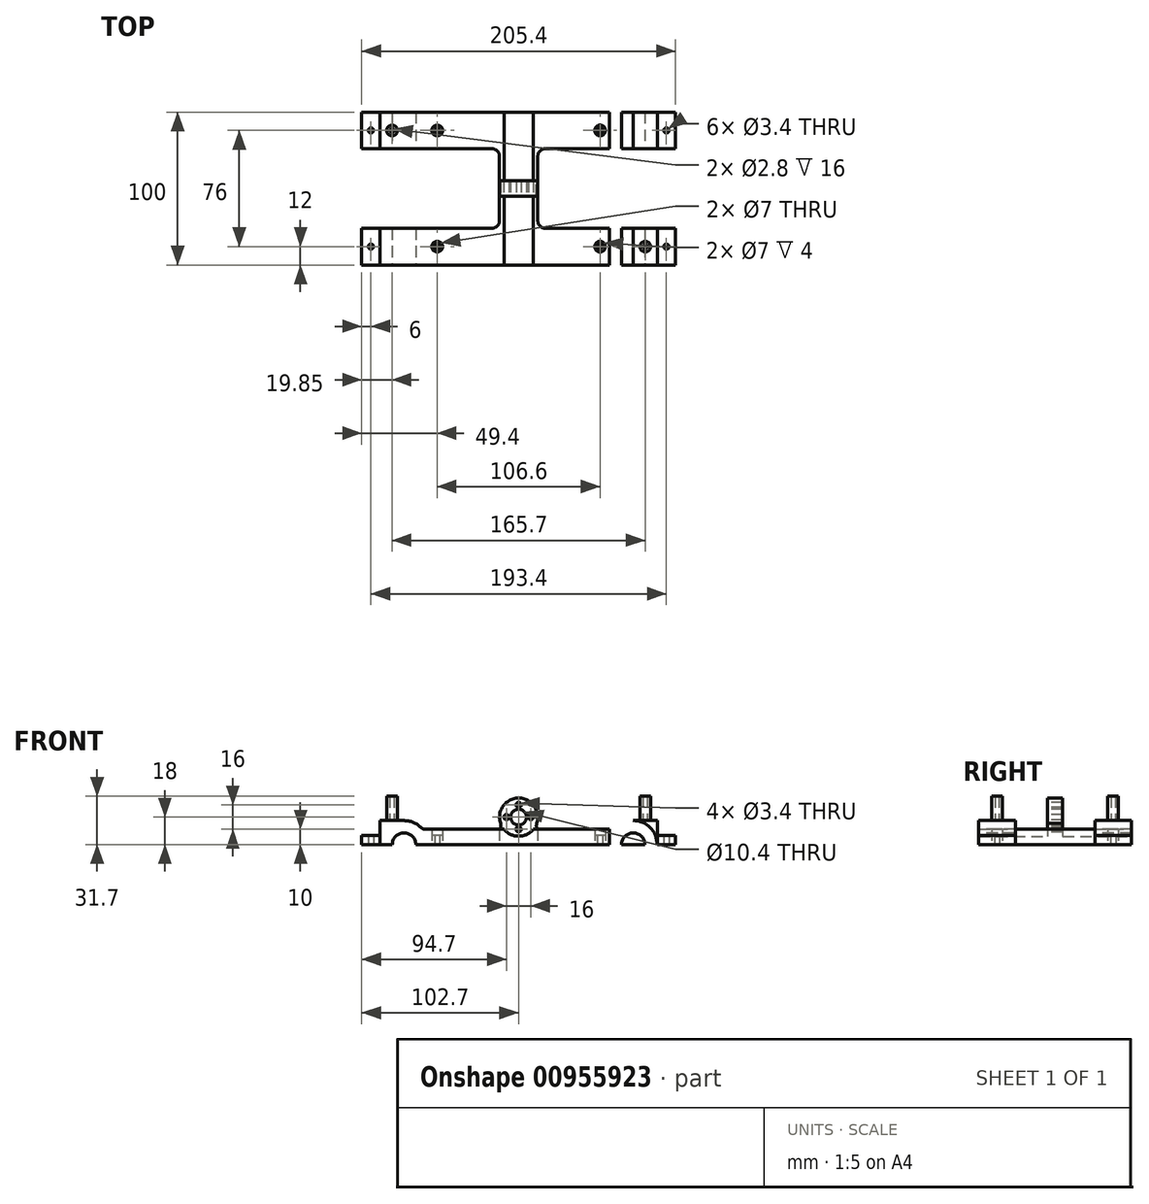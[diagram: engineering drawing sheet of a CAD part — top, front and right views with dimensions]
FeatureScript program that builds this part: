
annotation { "Feature Type Name" : "Feature", "Feature Type Description" : "" }
export const myFeature = defineFeature(function(context is Context, id is Id, definition is map)
    precondition{}
    {
        {
            var Q0;
            Q0=qCreatedBy(makeId("Top.planeOp"),FACE);
            var sketch = newSketch(context, id + "F0", { "sketchPlane" : qUnion([Q0])});
            skLineSegment(sketch, "E0", {"start": v(0, 0) * mm, "end": v(0, 50) * mm, "construction": true});
            skLineSegment(sketch, "E1", {"start": v(0, 0) * mm, "end": v(0, -50) * mm, "construction": true});
            skLineSegment(sketch, "E2", {"start": v(0, 50) * mm, "end": v(-59.3, 50) * mm});
            skLineSegment(sketch, "E3", {"start": v(-59.3, 50) * mm, "end": v(-59.3, 26) * mm});
            skLineSegment(sketch, "E4.bottom", {"start": v(-59.3, 26) * mm, "end": v(-90.7, 26) * mm});
            skLineSegment(sketch, "E4.top", {"start": v(-59.3, 50) * mm, "end": v(-90.7, 50) * mm});
            skLineSegment(sketch, "E4.left", {"start": v(-59.3, 26) * mm, "end": v(-59.3, 50) * mm});
            skLineSegment(sketch, "E4.right", {"start": v(-90.7, 26) * mm, "end": v(-90.7, 50) * mm});
            skLineSegment(sketch, "E5", {"start": v(-59.3, 26) * mm, "end": v(-12.5, 26) * mm});
            skLineSegment(sketch, "E6", {"start": v(0, 0) * mm, "end": v(-12.5, 0) * mm, "construction": true});
            skLineSegment(sketch, "E7", {"start": v(-12.5, 0) * mm, "end": v(-12.5, 26) * mm});
            skLineSegment(sketch, "E8.MirrorCS", {"start": v(59.3, 50) * mm, "end": v(90.7, 50) * mm});
            skLineSegment(sketch, "E9.MirrorCS", {"start": v(90.7, 26) * mm, "end": v(90.7, 50) * mm});
            skLineSegment(sketch, "E10.MirrorCS", {"start": v(59.3, 26) * mm, "end": v(90.7, 26) * mm});
            skLineSegment(sketch, "E11.MirrorCS", {"start": v(59.3, 26) * mm, "end": v(59.3, 50) * mm});
            skLineSegment(sketch, "E12.MirrorCS", {"start": v(59.3, 26) * mm, "end": v(12.5, 26) * mm});
            skLineSegment(sketch, "E13.MirrorCS", {"start": v(0, 50) * mm, "end": v(59.3, 50) * mm});
            skLineSegment(sketch, "E14.MirrorCS", {"start": v(12.5, 0) * mm, "end": v(12.5, 26) * mm});
            skLineSegment(sketch, "E15.MirrorCS", {"start": v(-12.5, 0) * mm, "end": v(-12.5, -26) * mm});
            skLineSegment(sketch, "E16.MirrorCS", {"start": v(-59.3, -26) * mm, "end": v(-12.5, -26) * mm});
            skLineSegment(sketch, "E17.MirrorCS", {"start": v(-59.3, -26) * mm, "end": v(-90.7, -26) * mm});
            skLineSegment(sketch, "E18.MirrorCS", {"start": v(-90.7, -26) * mm, "end": v(-90.7, -50) * mm});
            skLineSegment(sketch, "E19.MirrorCS", {"start": v(-59.3, -50) * mm, "end": v(-90.7, -50) * mm});
            skLineSegment(sketch, "E20.MirrorCS", {"start": v(-59.3, -26) * mm, "end": v(-59.3, -50) * mm});
            skLineSegment(sketch, "E21.MirrorCS", {"start": v(0, -50) * mm, "end": v(-59.3, -50) * mm});
            skLineSegment(sketch, "E22.MirrorCS", {"start": v(0, -50) * mm, "end": v(59.3, -50) * mm});
            skLineSegment(sketch, "E23.MirrorCS", {"start": v(59.3, -26) * mm, "end": v(12.5, -26) * mm});
            skLineSegment(sketch, "E24.MirrorCS", {"start": v(12.5, 0) * mm, "end": v(12.5, -26) * mm});
            skLineSegment(sketch, "E25.MirrorCS", {"start": v(59.3, -26) * mm, "end": v(90.7, -26) * mm});
            skLineSegment(sketch, "E26.MirrorCS", {"start": v(59.3, -26) * mm, "end": v(59.3, -50) * mm});
            skLineSegment(sketch, "E27.MirrorCS", {"start": v(59.3, -50) * mm, "end": v(90.7, -50) * mm});
            skLineSegment(sketch, "E28.MirrorCS", {"start": v(90.7, -26) * mm, "end": v(90.7, -50) * mm});
            skLineSegment(sketch, "E29.bottom", {"start": v(-12.5, 5) * mm, "end": v(12.5, 5) * mm});
            skLineSegment(sketch, "E29.top", {"start": v(-12.5, -5) * mm, "end": v(12.5, -5) * mm});
            skLineSegment(sketch, "E29.left", {"start": v(-12.5, 5) * mm, "end": v(-12.5, -5) * mm});
            skLineSegment(sketch, "E29.right", {"start": v(12.5, 5) * mm, "end": v(12.5, -5) * mm});
            skPoint(sketch, "E29.middle", {"position": v(0, 0) * mm});
            skLineSegment(sketch, "E30.bottom", {"start": v(-90.7, 50) * mm, "end": v(-99.7, 50) * mm});
            skLineSegment(sketch, "E30.top", {"start": v(-90.7, 26) * mm, "end": v(-99.7, 26) * mm});
            skLineSegment(sketch, "E30.left", {"start": v(-90.7, 50) * mm, "end": v(-90.7, 26) * mm});
            skCircle(sketch, "E31", {"center": v(-96.7, 38) * mm, "radius": 1.7 * mm});
            skPoint(sketch, "E31.centerSnap0", {"position": v(-90.7, 38) * mm});
            skPoint(sketch, "E31.centerSnap1", {"position": v(-96.7, 50) * mm});
            skLineSegment(sketch, "E32.MirrorCS", {"start": v(90.7, 50) * mm, "end": v(99.7, 50) * mm});
            skLineSegment(sketch, "E33.MirrorCS", {"start": v(90.7, 26) * mm, "end": v(99.7, 26) * mm});
            skLineSegment(sketch, "E34.MirrorCS", {"start": v(90.7, 50) * mm, "end": v(90.7, 26) * mm});
            skCircle(sketch, "E35.MirrorC", {"center": v(96.7, 38) * mm, "radius": 1.7 * mm});
            skCircle(sketch, "E36.MirrorC", {"center": v(-96.7, -38) * mm, "radius": 1.7 * mm});
            skLineSegment(sketch, "E37.MirrorCS", {"start": v(-90.7, -50) * mm, "end": v(-90.7, -26) * mm});
            skLineSegment(sketch, "E38.MirrorCS", {"start": v(-90.7, -50) * mm, "end": v(-99.7, -50) * mm});
            skLineSegment(sketch, "E39.MirrorCS", {"start": v(-90.7, -26) * mm, "end": v(-99.7, -26) * mm});
            skLineSegment(sketch, "E40.MirrorCS", {"start": v(90.7, -50) * mm, "end": v(90.7, -26) * mm});
            skLineSegment(sketch, "E41.MirrorCS", {"start": v(90.7, -50) * mm, "end": v(99.7, -50) * mm});
            skLineSegment(sketch, "E42.MirrorCS", {"start": v(90.7, -26) * mm, "end": v(99.7, -26) * mm});
            skCircle(sketch, "E43.MirrorC", {"center": v(96.7, -38) * mm, "radius": 1.7 * mm});
            skLineSegment(sketch, "E44", {"start": v(-59.3, 38) * mm, "end": v(-53.3, 38) * mm, "construction": true});
            skCircle(sketch, "E45", {"center": v(-53.3, 38) * mm, "radius": 1.7 * mm});
            skCircle(sketch, "E46.MirrorC", {"center": v(53.3, 38) * mm, "radius": 1.7 * mm});
            skCircle(sketch, "E47.MirrorC", {"center": v(-53.3, -38) * mm, "radius": 1.7 * mm});
            skCircle(sketch, "E48.MirrorC", {"center": v(53.3, -38) * mm, "radius": 1.7 * mm});
            skCircle(sketch, "E49", {"center": v(-53.3, 38) * mm, "radius": 3.5 * mm});
            skCircle(sketch, "E50.MirrorC", {"center": v(53.3, 38) * mm, "radius": 3.5 * mm});
            skCircle(sketch, "E51.MirrorC", {"center": v(-53.3, -38) * mm, "radius": 3.5 * mm});
            skCircle(sketch, "E52.MirrorC", {"center": v(53.3, -38) * mm, "radius": 3.5 * mm});
            skLineSegment(sketch, "E53", {"start": v(-12.5, 0) * mm, "end": v(-60.78, 0) * mm, "construction": true});
            skLineSegment(sketch, "E54", {"start": v(-96.7, -38) * mm, "end": v(-90.7, -38) * mm, "construction": true});
            skLineSegment(sketch, "E55", {"start": v(-96.7, 38) * mm, "end": v(-90.7, 38) * mm, "construction": true});
            skPoint(sketch, "E56.orphan", {"position": v(-102.7, 26) * mm});
            skPoint(sketch, "E57.orphan", {"position": v(-102.7, 50) * mm});
            skPoint(sketch, "E58.MirrorCS.end.orphan", {"position": v(-102.7, -26) * mm});
            skPoint(sketch, "E58.MirrorCS.start.orphan", {"position": v(-102.7, -50) * mm});
            skPoint(sketch, "E59.orphan", {"position": v(102.7, -26) * mm});
            skPoint(sketch, "E60.MirrorCS.start.orphan", {"position": v(102.7, -50) * mm});
            skPoint(sketch, "E61.orphan", {"position": v(102.7, 26) * mm});
            skPoint(sketch, "E62.MirrorCS.start.orphan", {"position": v(102.7, 50) * mm});
            skLineSegment(sketch, "E63", {"start": v(-102.7, 50) * mm, "end": v(-99.7, 50) * mm});
            skLineSegment(sketch, "E64", {"start": v(-102.7, 50) * mm, "end": v(-102.7, 26) * mm});
            skLineSegment(sketch, "E65", {"start": v(-102.7, 26) * mm, "end": v(-99.7, 26) * mm});
            skLineSegment(sketch, "E66.MirrorCS", {"start": v(102.7, 50) * mm, "end": v(102.7, 26) * mm});
            skLineSegment(sketch, "E67.MirrorCS", {"start": v(102.7, 26) * mm, "end": v(99.7, 26) * mm});
            skLineSegment(sketch, "E68.MirrorCS", {"start": v(102.7, 50) * mm, "end": v(99.7, 50) * mm});
            skLineSegment(sketch, "E69.MirrorCS", {"start": v(102.7, -26) * mm, "end": v(99.7, -26) * mm});
            skLineSegment(sketch, "E70.MirrorCS", {"start": v(102.7, -50) * mm, "end": v(102.7, -26) * mm});
            skLineSegment(sketch, "E71.MirrorCS", {"start": v(102.7, -50) * mm, "end": v(99.7, -50) * mm});
            skLineSegment(sketch, "E72.MirrorCS", {"start": v(-102.7, -50) * mm, "end": v(-99.7, -50) * mm});
            skLineSegment(sketch, "E73.MirrorCS", {"start": v(-102.7, -50) * mm, "end": v(-102.7, -26) * mm});
            skLineSegment(sketch, "E74.MirrorCS", {"start": v(-102.7, -26) * mm, "end": v(-99.7, -26) * mm});
            skSolve(sketch);
        }
        {
            var Q0;
            Q0=makeQuery(id+"F0.imprint","IMPRINT",FACE,{"disambiguationData":[TD([[makeQuery(id+"F0.imprint","IMPRINT",EDGE,{"derivedFrom":sQuery(id+"F0.wireOp",EDGE,"E2")}),1.0]])]});
            var Q1;
            {var subQ4=sQuery(id+"F0.wireOp",EDGE,"E16.MirrorCS");Q1=makeQuery(id+"F0.imprint","IMPRINT",FACE,{"disambiguationData":[TD([[makeQuery(id+"F0.imprint","IMPRINT",EDGE,{"derivedFrom":subQ4}),-1.0]])]});}
            extrude(context, id + "F1", {"entities" : qUnion([Q0, Q1]), "depth" : 10 * mm});
        }
        {
            var Q0;
            Q0=makeQuery(id+"F0.imprint","IMPRINT",FACE,{"disambiguationData":[TD([[makeQuery(id+"F0.imprint","IMPRINT",EDGE,{"derivedFrom":sQuery(id+"F0.wireOp",EDGE,"E17.MirrorCS")}),1.0]])]});
            var Q1;
            Q1=makeQuery(id+"F0.imprint","IMPRINT",FACE,{"disambiguationData":[TD([[makeQuery(id+"F0.imprint","IMPRINT",EDGE,{"derivedFrom":sQuery(id+"F0.wireOp",EDGE,"E3")}),-1.0]])]});
            var Q2;
            Q2=makeQuery(id+"F0.imprint","IMPRINT",FACE,{"disambiguationData":[TD([[makeQuery(id+"F0.imprint","IMPRINT",EDGE,{"derivedFrom":sQuery(id+"F0.wireOp",EDGE,"E8.MirrorCS")}),-1.0]])]});
            var Q3;
            Q3=makeQuery(id+"F0.imprint","IMPRINT",FACE,{"disambiguationData":[TD([[makeQuery(id+"F0.imprint","IMPRINT",EDGE,{"derivedFrom":sQuery(id+"F0.wireOp",EDGE,"E25.MirrorCS")}),-1.0]])]});
            extrude(context, id + "F2", {"entities" : qUnion([Q0, Q1, Q2, Q3]), "depth" : 15.7 * mm});
        }
        {
            var Q0;
            {var subQ0=sQuery(id+"F0.wireOp",EDGE,"E29.bottom");Q0=makeQuery(id+"F0.imprint","IMPRINT",FACE,{"disambiguationData":[TD([[makeQuery(id+"F0.imprint","IMPRINT",EDGE,{"derivedFrom":subQ0}),-1.0]])]});}
            extrude(context, id + "F3", {"entities" : qUnion([Q0]), "depth" : 30.5 * mm});
        }
        {
            var Q0;
            Q0=makeQuery(id+"F2.opExtrude","SWEPT_BODY",BODY,{"disambiguationData":[OSD([sQuery(id+"F0.wireOp",EDGE,"E25.MirrorCS"),sQuery(id+"F0.wireOp",EDGE,"E26.MirrorCS"),sQuery(id+"F0.wireOp",EDGE,"E27.MirrorCS"),sQuery(id+"F0.wireOp",EDGE,"E28.MirrorCS")])]});
            var Q1;
            Q1=makeQuery(id+"F2.opExtrude","SWEPT_BODY",BODY,{"disambiguationData":[OSD([sQuery(id+"F0.wireOp",EDGE,"E3"),sQuery(id+"F0.wireOp",EDGE,"E4.bottom"),sQuery(id+"F0.wireOp",EDGE,"E4.top"),sQuery(id+"F0.wireOp",EDGE,"E4.right")])]});
            var Q2;
            Q2=makeQuery(id+"F2.opExtrude","SWEPT_BODY",BODY,{"disambiguationData":[OSD([sQuery(id+"F0.wireOp",EDGE,"E17.MirrorCS"),sQuery(id+"F0.wireOp",EDGE,"E18.MirrorCS"),sQuery(id+"F0.wireOp",EDGE,"E19.MirrorCS"),sQuery(id+"F0.wireOp",EDGE,"E20.MirrorCS")])]});
            var Q3;
            Q3=makeQuery(id+"F1.opExtrude","SWEPT_BODY",BODY,{"disambiguationData":[OSD([sQuery(id+"F0.wireOp",EDGE,"E2"),sQuery(id+"F0.wireOp",EDGE,"E3"),sQuery(id+"F0.wireOp",EDGE,"E5"),sQuery(id+"F0.wireOp",EDGE,"E7"),sQuery(id+"F0.wireOp",EDGE,"E11.MirrorCS"),sQuery(id+"F0.wireOp",EDGE,"E12.MirrorCS"),sQuery(id+"F0.wireOp",EDGE,"E13.MirrorCS"),sQuery(id+"F0.wireOp",EDGE,"E14.MirrorCS"),sQuery(id+"F0.wireOp",EDGE,"E29.bottom"),sQuery(id+"F0.wireOp",EDGE,"E49"),sQuery(id+"F0.wireOp",EDGE,"E50.MirrorC")])]});
            var Q4;
            Q4=makeQuery(id+"F1.opExtrude","SWEPT_BODY",BODY,{"disambiguationData":[OSD([sQuery(id+"F0.wireOp",EDGE,"E15.MirrorCS"),sQuery(id+"F0.wireOp",EDGE,"E16.MirrorCS"),sQuery(id+"F0.wireOp",EDGE,"E20.MirrorCS"),sQuery(id+"F0.wireOp",EDGE,"E21.MirrorCS"),sQuery(id+"F0.wireOp",EDGE,"E22.MirrorCS"),sQuery(id+"F0.wireOp",EDGE,"E23.MirrorCS"),sQuery(id+"F0.wireOp",EDGE,"E24.MirrorCS"),sQuery(id+"F0.wireOp",EDGE,"E26.MirrorCS"),sQuery(id+"F0.wireOp",EDGE,"E29.top"),sQuery(id+"F0.wireOp",EDGE,"E51.MirrorC"),sQuery(id+"F0.wireOp",EDGE,"E52.MirrorC")])]});
            var Q5;
            Q5=makeQuery(id+"F3.opExtrude","SWEPT_BODY",BODY,{"disambiguationData":[OSD([sQuery(id+"F0.wireOp",EDGE,"E7"),sQuery(id+"F0.wireOp",EDGE,"E24.MirrorCS"),sQuery(id+"F0.wireOp",EDGE,"E29.bottom"),sQuery(id+"F0.wireOp",EDGE,"E29.top")])]});
            var Q6;
            Q6=makeQuery(id+"F2.opExtrude","SWEPT_BODY",BODY,{"disambiguationData":[OSD([sQuery(id+"F0.wireOp",EDGE,"E8.MirrorCS"),sQuery(id+"F0.wireOp",EDGE,"E9.MirrorCS"),sQuery(id+"F0.wireOp",EDGE,"E10.MirrorCS"),sQuery(id+"F0.wireOp",EDGE,"E11.MirrorCS")])]});
            booleanBodies(context, id + "F4", {"operationType" : BooleanOperationType.UNION, "tools" : qUnion([Q0, Q1, Q2, Q3, Q4, Q5, Q6])});
        }
        {
            var Q0;
            Q0=makeQuery(id+"F4.opBoolean","MERGE",FACE,{"derivedFrom":[makeQuery(id+"F1.opExtrude","SWEPT_FACE",FACE,{"disambiguationData":[OSD([sQuery(id+"F0.wireOp",EDGE,"E21.MirrorCS"),sQuery(id+"F0.wireOp",EDGE,"E22.MirrorCS")])]}),makeQuery(id+"F2.opExtrude","SWEPT_FACE",FACE,{"disambiguationData":[OSD([sQuery(id+"F0.wireOp",EDGE,"E19.MirrorCS")])]}),makeQuery(id+"F2.opExtrude","SWEPT_FACE",FACE,{"disambiguationData":[OSD([sQuery(id+"F0.wireOp",EDGE,"E27.MirrorCS")])]})]});
            var sketch = newSketch(context, id + "F5", { "sketchPlane" : qUnion([Q0])});
            skLineSegment(sketch, "E75", {"start": v(-75, 15.7) * mm, "end": v(-75, 0) * mm, "construction": true});
            skArc(sketch, "E76", {"start": v(-64.07, 11.27) * mm, "mid": v(-81.12, 14.46) * mm, "end": v(-90.7, 0) * mm});
            skArc(sketch, "E77", {"start": v(-67.3, 0) * mm, "mid": v(-75, 7.7) * mm, "end": v(-82.7, 0) * mm});
            skLineSegment(sketch, "E78", {"start": v(-82.7, 0) * mm, "end": v(-90.7, 0) * mm});
            skLineSegment(sketch, "E79", {"start": v(-67.3, 0) * mm, "end": v(-59.3, 0) * mm});
            skLineSegment(sketch, "E80", {"start": v(0, 0) * mm, "end": v(0, 35.4) * mm, "construction": true});
            skPoint(sketch, "E80.endSnap0", {"position": v(0, 0) * mm});
            skArc(sketch, "E81.MirrorCS", {"start": v(67.3, 0) * mm, "mid": v(75, 7.7) * mm, "end": v(82.7, 0) * mm});
            skLineSegment(sketch, "E82.MirrorCS", {"start": v(82.7, 0) * mm, "end": v(90.7, 0) * mm});
            skArc(sketch, "E83.MirrorCS", {"start": v(64.07, 11.27) * mm, "mid": v(81.12, 14.46) * mm, "end": v(90.7, 0) * mm});
            skLineSegment(sketch, "E84.MirrorCS", {"start": v(67.3, 0) * mm, "end": v(59.3, 0) * mm});
            skLineSegment(sketch, "E85", {"start": v(-59.3, 0) * mm, "end": v(-59.3, 15.7) * mm});
            skLineSegment(sketch, "E86", {"start": v(-59.3, 15.7) * mm, "end": v(-75, 15.7) * mm});
            skLineSegment(sketch, "E87.MirrorCS", {"start": v(59.3, 15.7) * mm, "end": v(75, 15.7) * mm});
            skLineSegment(sketch, "E88.MirrorCS", {"start": v(59.3, 0) * mm, "end": v(59.3, 15.7) * mm});
            skLineSegment(sketch, "E89", {"start": v(-59.3, 10) * mm, "end": v(-60.94, 10) * mm});
            skPoint(sketch, "E90.newPointA", {"position": v(-59.3, 0) * mm});
            skArc(sketch, "E90.filletArc", {"start": v(-64.07, 11.27) * mm, "mid": v(-62.63, 10.33) * mm, "end": v(-60.94, 10) * mm});
            skLineSegment(sketch, "E91", {"start": v(59.3, 10) * mm, "end": v(60.94, 10) * mm});
            skPoint(sketch, "E92.newPointB", {"position": v(59.3, 0) * mm});
            skArc(sketch, "E92.filletArc", {"start": v(60.94, 10) * mm, "mid": v(62.63, 10.33) * mm, "end": v(64.07, 11.27) * mm});
            skSolve(sketch);
        }
        {
            var Q0;
            {var subQ6=sQuery(id+"F5.wireOp",EDGE,"E87.MirrorCS");Q0=makeQuery(id+"F5.imprint","IMPRINT",FACE,{"disambiguationData":[TD([[makeQuery(id+"F5.imprint","IMPRINT",EDGE,{"derivedFrom":subQ6}),-1.0]])]});}
            var Q1;
            {var subQ0=sQuery(id+"F5.wireOp",EDGE,"8ee72258-81a3-4149-ab89-0d706ac254500.MirrorCS");Q1=makeQuery(id+"F5.imprint","IMPRINT",FACE,{"disambiguationData":[TD([[makeQuery(id+"F5.imprint","IMPRINT",EDGE,{"derivedFrom":subQ0}),-1.0]])]});}
            var Q2;
            {var subQ0=sQuery(id+"F5.wireOp",EDGE,"E81.MirrorCS");Q2=makeQuery(id+"F5.imprint","IMPRINT",FACE,{"disambiguationData":[TD([[makeQuery(id+"F5.imprint","IMPRINT",EDGE,{"derivedFrom":subQ0}),-1.0]])]});}
            var Q3;
            {var subQ0=sQuery(id+"F5.wireOp",EDGE,"2AFTPnqg-4Tv1-YmLw-YE9B-kkPoXeHdkq1D");Q3=makeQuery(id+"F5.imprint","IMPRINT",FACE,{"disambiguationData":[TD([[makeQuery(id+"F5.imprint","IMPRINT",EDGE,{"derivedFrom":subQ0}),1.0]])]});}
            var Q4;
            {var subQ6=sQuery(id+"F5.wireOp",EDGE,"E86");Q4=makeQuery(id+"F5.imprint","IMPRINT",FACE,{"disambiguationData":[TD([[makeQuery(id+"F5.imprint","IMPRINT",EDGE,{"derivedFrom":subQ6}),1.0]])]});}
            var Q5;
            {var subQ0=sQuery(id+"F5.wireOp",EDGE,"E77");Q5=makeQuery(id+"F5.imprint","IMPRINT",FACE,{"disambiguationData":[TD([[makeQuery(id+"F5.imprint","IMPRINT",EDGE,{"derivedFrom":subQ0}),1.0]])]});}
            extrude(context, id + "F6", {"entities" : qUnion([Q0, Q1, Q2, Q3, Q4, Q5]), "operationType" : NewBodyOperationType.REMOVE, "oppositeDirection" : true, "depth" : 100 * mm});
        }
        {
            var Q0;
            Q0=makeQuery(id+"F3.opExtrude","SWEPT_FACE",FACE,{"disambiguationData":[OSD([sQuery(id+"F0.wireOp",EDGE,"E29.top")])]});
            var sketch = newSketch(context, id + "F7", { "sketchPlane" : qUnion([Q0])});
            skLineSegment(sketch, "E93", {"start": v(0, 0) * mm, "end": v(0, 18) * mm, "construction": true});
            skFitSpline(sketch, "E94", {"points": [v(-11.82, 13.93) * mm, v(-11.66, 11.67) * mm, v(-12.5, 10) * mm], "startDerivative": vector(0.82, -4.52) * mm, "endDerivative": vector(-2.25, -3.32) * mm});
            skFitSpline(sketch, "E95.MirrorCS", {"points": [v(11.82, 13.93) * mm, v(11.66, 11.67) * mm, v(12.5, 10) * mm], "startDerivative": vector(-0.82, -4.52) * mm, "endDerivative": vector(2.25, -3.32) * mm});
            skCircle(sketch, "E96", {"center": v(0, 18) * mm, "radius": 5.2 * mm});
            skCircle(sketch, "E97", {"center": v(0, 18) * mm, "radius": 8 * mm, "construction": true});
            skArc(sketch, "E98", {"start": v(11.82, 13.93) * mm, "mid": v(0, 30.5) * mm, "end": v(-11.82, 13.93) * mm});
            skCircle(sketch, "E99", {"center": v(0, 26) * mm, "radius": 1.7 * mm});
            skCircle(sketch, "E100", {"center": v(8, 18) * mm, "radius": 1.7 * mm});
            skCircle(sketch, "E101", {"center": v(0, 10) * mm, "radius": 1.7 * mm});
            skCircle(sketch, "E102", {"center": v(-8, 18) * mm, "radius": 1.7 * mm});
            skLineSegment(sketch, "E103", {"start": v(-12.5, 10) * mm, "end": v(-9.6, 10) * mm});
            skLineSegment(sketch, "E104", {"start": v(12.5, 10) * mm, "end": v(9.6, 10) * mm});
            skArc(sketch, "E105.trimOffspring", {"start": v(-9.6, 10) * mm, "mid": v(0, 5.5) * mm, "end": v(9.6, 10) * mm});
            skSolve(sketch);
        }
        {
            var Q0;
            {var subQ0=sQuery(id+"F7.wireOp",EDGE,"E98");var subQ1=sQuery(id+"F0.wireOp",EDGE,"E29.top");var subQ2=makeQuery(id+"F3.opExtrude","CAP_EDGE",EDGE,{"disambiguationData":[OSD([subQ1])],"isStart":false});var subQ3=makeQuery(id+"F7.imprint","INTERSECT",VERTEX,{"derivedFrom":[subQ2,subQ0]});Q0=makeQuery(id+"F7.imprint","IMPRINT",FACE,{"disambiguationData":[TD([[makeQuery(id+"F7.imprint","IMPRINT",EDGE,{"disambiguationData":[TD([[subQ3,-1.0]])],"derivedFrom":subQ0}),-1.0]])]});}
            var Q1;
            {var subQ0=sQuery(id+"F7.wireOp",EDGE,"E98");var subQ1=sQuery(id+"F0.wireOp",EDGE,"E29.top");var subQ4=makeQuery(id+"F3.opExtrude","CAP_EDGE",EDGE,{"disambiguationData":[OSD([subQ1])],"isStart":false});var subQ5=makeQuery(id+"F7.imprint","INTERSECT",VERTEX,{"derivedFrom":[subQ4,subQ0]});Q1=makeQuery(id+"F7.imprint","IMPRINT",FACE,{"disambiguationData":[TD([[makeQuery(id+"F7.imprint","IMPRINT",EDGE,{"disambiguationData":[TD([[subQ5,1.0]])],"derivedFrom":subQ0}),-1.0]])]});}
            var Q2;
            {var subQ0=sQuery(id+"F7.wireOp",EDGE,"E94");Q2=makeQuery(id+"F7.imprint","IMPRINT",FACE,{"disambiguationData":[TD([[makeQuery(id+"F7.imprint","IMPRINT",EDGE,{"derivedFrom":subQ0}),-1.0]])]});}
            var Q3;
            {var subQ0=sQuery(id+"F7.wireOp",EDGE,"E95.MirrorCS");Q3=makeQuery(id+"F7.imprint","IMPRINT",FACE,{"disambiguationData":[TD([[makeQuery(id+"F7.imprint","IMPRINT",EDGE,{"derivedFrom":subQ0}),1.0]])]});}
            var Q4;
            Q4=makeQuery(id+"F7.imprint","IMPRINT",FACE,{"disambiguationData":[TD([[makeQuery(id+"F7.imprint","IMPRINT",EDGE,{"derivedFrom":sQuery(id+"F7.wireOp",EDGE,"E102")}),1.0]])]});
            var Q5;
            Q5=makeQuery(id+"F7.imprint","IMPRINT",FACE,{"disambiguationData":[TD([[makeQuery(id+"F7.imprint","IMPRINT",EDGE,{"derivedFrom":sQuery(id+"F7.wireOp",EDGE,"E99")}),1.0]])]});
            var Q6;
            Q6=makeQuery(id+"F7.imprint","IMPRINT",FACE,{"disambiguationData":[TD([[makeQuery(id+"F7.imprint","IMPRINT",EDGE,{"derivedFrom":sQuery(id+"F7.wireOp",EDGE,"E100")}),1.0]])]});
            var Q7;
            {var subQ0=sQuery(id+"F7.wireOp",EDGE,"E101");var subQ1=makeQuery(id+"F1.opExtrude","CAP_EDGE",EDGE,{"disambiguationData":[OSD([sQuery(id+"F0.wireOp",EDGE,"E29.top")])],"isStart":false});var subQ2=makeQuery(id+"F7.imprint","INTERSECT",VERTEX,{"disambiguationData":[OD(0.0)],"derivedFrom":[subQ1,subQ0]});Q7=makeQuery(id+"F7.imprint","IMPRINT",FACE,{"disambiguationData":[TD([[makeQuery(id+"F7.imprint","IMPRINT",EDGE,{"disambiguationData":[TD([[subQ2,1.0]])],"derivedFrom":subQ0}),1.0]])]});}
            var Q8;
            {var subQ0=sQuery(id+"F7.wireOp",EDGE,"E101");var subQ1=makeQuery(id+"F1.opExtrude","CAP_EDGE",EDGE,{"disambiguationData":[OSD([sQuery(id+"F0.wireOp",EDGE,"E29.top")])],"isStart":false});var subQ2=makeQuery(id+"F7.imprint","INTERSECT",VERTEX,{"disambiguationData":[OD(0.0)],"derivedFrom":[subQ1,subQ0]});Q8=makeQuery(id+"F7.imprint","IMPRINT",FACE,{"disambiguationData":[TD([[makeQuery(id+"F7.imprint","IMPRINT",EDGE,{"disambiguationData":[TD([[subQ2,-1.0]])],"derivedFrom":subQ0}),1.0]])]});}
            var Q9;
            Q9=makeQuery(id+"F7.imprint","IMPRINT",FACE,{"disambiguationData":[TD([[makeQuery(id+"F7.imprint","IMPRINT",EDGE,{"derivedFrom":sQuery(id+"F7.wireOp",EDGE,"E96")}),1.0]])]});
            extrude(context, id + "F8", {"entities" : qUnion([Q0, Q1, Q2, Q3, Q4, Q5, Q6, Q7, Q8, Q9]), "operationType" : NewBodyOperationType.REMOVE, "endBound" : BoundingType.SYMMETRIC, "oppositeDirection" : true, "depth" : 120 * mm});
        }
        {
            var Q0;
            {var subQ4=sQuery(id+"F7.wireOp",EDGE,"E105.trimOffspring");Q0=makeQuery(id+"F7.imprint","IMPRINT",FACE,{"disambiguationData":[TD([[makeQuery(id+"F7.imprint","IMPRINT",EDGE,{"derivedFrom":subQ4}),1.0]])]});}
            extrude(context, id + "F9", {"entities" : qUnion([Q0]), "operationType" : NewBodyOperationType.REMOVE, "depth" : 100 * mm});
        }
        {
            var Q0;
            {var subQ4=sQuery(id+"F7.wireOp",EDGE,"E105.trimOffspring");Q0=makeQuery(id+"F7.imprint","IMPRINT",FACE,{"disambiguationData":[TD([[makeQuery(id+"F7.imprint","IMPRINT",EDGE,{"derivedFrom":subQ4}),1.0]])]});}
            extrude(context, id + "F10", {"entities" : qUnion([Q0]), "operationType" : NewBodyOperationType.REMOVE, "oppositeDirection" : true, "depth" : 100 * mm});
        }
        {
            var Q0;
            {var subQ4=sQuery(id+"F7.wireOp",EDGE,"E105.trimOffspring");Q0=makeQuery(id+"F7.imprint","IMPRINT",FACE,{"disambiguationData":[TD([[makeQuery(id+"F7.imprint","IMPRINT",EDGE,{"derivedFrom":subQ4}),1.0]])]});}
            extrude(context, id + "F11", {"entities" : qUnion([Q0]), "operationType" : NewBodyOperationType.ADD, "oppositeDirection" : true, "depth" : 10 * mm});
        }
        {
            var Q0;
            Q0=makeQuery(id+"F1.opExtrude","SWEPT_EDGE",EDGE,{"disambiguationData":[OSD([sQuery(id+"F0.wireOp",EDGE,"E5"),sQuery(id+"F0.wireOp",EDGE,"E7")])]});
            var Q1;
            Q1=makeQuery(id+"F1.opExtrude","SWEPT_EDGE",EDGE,{"disambiguationData":[OSD([sQuery(id+"F0.wireOp",EDGE,"E12.MirrorCS"),sQuery(id+"F0.wireOp",EDGE,"E14.MirrorCS")])]});
            var Q2;
            Q2=makeQuery(id+"F1.opExtrude","SWEPT_EDGE",EDGE,{"disambiguationData":[OSD([sQuery(id+"F0.wireOp",EDGE,"E15.MirrorCS"),sQuery(id+"F0.wireOp",EDGE,"E16.MirrorCS")])]});
            var Q3;
            Q3=makeQuery(id+"F1.opExtrude","SWEPT_EDGE",EDGE,{"disambiguationData":[OSD([sQuery(id+"F0.wireOp",EDGE,"E23.MirrorCS"),sQuery(id+"F0.wireOp",EDGE,"E24.MirrorCS")])]});
            fillet(context, id + "F12", {"entities" : qUnion([Q0, Q1, Q2, Q3]), "radius" : 5 * mm, "tangentPropagation" : true, "allowEdgeOverflow" : false});
        }
        {
            var Q0;
            Q0=makeQuery(id+"F0.imprint","IMPRINT",FACE,{"disambiguationData":[TD([[makeQuery(id+"F0.imprint","IMPRINT",EDGE,{"derivedFrom":sQuery(id+"F0.wireOp",EDGE,"E4.right")}),1.0]])]});
            var Q1;
            Q1=makeQuery(id+"F0.imprint","IMPRINT",FACE,{"disambiguationData":[TD([[makeQuery(id+"F0.imprint","IMPRINT",EDGE,{"derivedFrom":sQuery(id+"F0.wireOp",EDGE,"E18.MirrorCS")}),-1.0]])]});
            var Q2;
            Q2=makeQuery(id+"F0.imprint","IMPRINT",FACE,{"disambiguationData":[TD([[makeQuery(id+"F0.imprint","IMPRINT",EDGE,{"derivedFrom":sQuery(id+"F0.wireOp",EDGE,"E28.MirrorCS")}),1.0]])]});
            var Q3;
            Q3=makeQuery(id+"F0.imprint","IMPRINT",FACE,{"disambiguationData":[TD([[makeQuery(id+"F0.imprint","IMPRINT",EDGE,{"derivedFrom":sQuery(id+"F0.wireOp",EDGE,"E9.MirrorCS")}),-1.0]])]});
            extrude(context, id + "F13", {"entities" : qUnion([Q0, Q1, Q2, Q3]), "depth" : 6 * mm});
        }
        {
            var Q0;
            Q0=makeQuery(id+"F0.imprint","IMPRINT",FACE,{"disambiguationData":[TD([[makeQuery(id+"F0.imprint","IMPRINT",EDGE,{"derivedFrom":sQuery(id+"F0.wireOp",EDGE,"E45")}),-1.0]])]});
            var Q1;
            Q1=makeQuery(id+"F0.imprint","IMPRINT",FACE,{"disambiguationData":[TD([[makeQuery(id+"F0.imprint","IMPRINT",EDGE,{"derivedFrom":sQuery(id+"F0.wireOp",EDGE,"E46.MirrorC")}),1.0]])]});
            var Q2;
            Q2=makeQuery(id+"F0.imprint","IMPRINT",FACE,{"disambiguationData":[TD([[makeQuery(id+"F0.imprint","IMPRINT",EDGE,{"derivedFrom":sQuery(id+"F0.wireOp",EDGE,"E47.MirrorC")}),1.0]])]});
            var Q3;
            Q3=makeQuery(id+"F0.imprint","IMPRINT",FACE,{"disambiguationData":[TD([[makeQuery(id+"F0.imprint","IMPRINT",EDGE,{"derivedFrom":sQuery(id+"F0.wireOp",EDGE,"E48.MirrorC")}),-1.0]])]});
            extrude(context, id + "F14", {"entities" : qUnion([Q0, Q1, Q2, Q3]), "operationType" : NewBodyOperationType.ADD, "depth" : 6 * mm});
        }
        {
            var Q0;
            Q0=makeQuery(id+"F2.opExtrude","CAP_FACE",FACE,{"disambiguationData":[OSD([sQuery(id+"F0.wireOp",EDGE,"E3"),sQuery(id+"F0.wireOp",EDGE,"E4.bottom"),sQuery(id+"F0.wireOp",EDGE,"E4.top"),sQuery(id+"F0.wireOp",EDGE,"E4.right")])],"isStart":false});
            var sketch = newSketch(context, id + "F15", { "sketchPlane" : qUnion([Q0])});
            skLineSegment(sketch, "E106", {"start": v(-90.7, 50) * mm, "end": v(-75, 26) * mm, "construction": true});
            skLineSegment(sketch, "E107", {"start": v(-75, 50) * mm, "end": v(-90.7, 26) * mm, "construction": true});
            skCircle(sketch, "E108", {"center": v(-82.85, 38) * mm, "radius": 3.5 * mm});
            skLineSegment(sketch, "E109", {"start": v(0, 0) * mm, "end": v(0, 47.66) * mm, "construction": true});
            skLineSegment(sketch, "E110", {"start": v(0, 0) * mm, "end": v(-18.82, 0) * mm, "construction": true});
            skCircle(sketch, "E111.MirrorC", {"center": v(82.85, 38) * mm, "radius": 3.5 * mm});
            skCircle(sketch, "E112.MirrorC", {"center": v(-82.85, -38) * mm, "radius": 3.5 * mm});
            skCircle(sketch, "E113.MirrorC", {"center": v(82.85, -38) * mm, "radius": 3.5 * mm});
            skCircle(sketch, "E114", {"center": v(-82.85, -38) * mm, "radius": 1.4 * mm});
            skCircle(sketch, "E115.MirrorC", {"center": v(82.85, -38) * mm, "radius": 1.4 * mm});
            skCircle(sketch, "E116.MirrorC", {"center": v(-82.85, 38) * mm, "radius": 1.4 * mm});
            skCircle(sketch, "E117.MirrorC", {"center": v(82.85, 38) * mm, "radius": 1.4 * mm});
            skLineSegment(sketch, "E118", {"start": v(-18.82, 0) * mm, "end": v(-113.22, 0) * mm, "construction": true});
            skSolve(sketch);
        }
        {
            var Q0;
            Q0=makeQuery(id+"F15.imprint","IMPRINT",FACE,{"disambiguationData":[TD([[makeQuery(id+"F15.imprint","IMPRINT",EDGE,{"derivedFrom":sQuery(id+"F15.wireOp",EDGE,"E108")}),1.0]])]});
            var Q1;
            Q1=makeQuery(id+"F15.imprint","IMPRINT",FACE,{"disambiguationData":[TD([[makeQuery(id+"F15.imprint","IMPRINT",EDGE,{"derivedFrom":sQuery(id+"F15.wireOp",EDGE,"E111.MirrorC")}),-1.0]])]});
            var Q2;
            Q2=makeQuery(id+"F15.imprint","IMPRINT",FACE,{"disambiguationData":[TD([[makeQuery(id+"F15.imprint","IMPRINT",EDGE,{"derivedFrom":sQuery(id+"F15.wireOp",EDGE,"E113.MirrorC")}),1.0]])]});
            var Q3;
            Q3=makeQuery(id+"F15.imprint","IMPRINT",FACE,{"disambiguationData":[TD([[makeQuery(id+"F15.imprint","IMPRINT",EDGE,{"derivedFrom":sQuery(id+"F15.wireOp",EDGE,"E112.MirrorC")}),-1.0]])]});
            extrude(context, id + "F16", {"entities" : qUnion([Q0, Q1, Q2, Q3]), "operationType" : NewBodyOperationType.ADD, "depth" : 16 * mm});
        }
    });
